# Revit family: Grohe_PlumbingFixtures_RapidoSmartBox_UniversalRoughInBox_35600000_Metric1
name_source: partatom
category: Plumbing Fixtures
revit_build: Autodesk Revit 2016 (Build: 20150714_1515(x64)
units: mm (PartAtom-declared; Revit-internal decimal feet)

## family parameters
Cut with Voids When Loaded = No
Host = Face
OmniClass Number = 23.45.55.17
OmniClass Title = Mixing Faucets
Part Type = Normal
Room Calculation Point = No
Round Connector Dimension = Use Diameter
Shared = Yes

## types (1)
- 35600000
    ADACompliant = No
    Assembly Code = D2010
    AssetType = Fixed
    BIMObjectName = Grohe_PlumbingFixtures_RapidoSmartBox_UniversalRoughInBox_35600000_Metric
    CW Connection = Yes
    CWFU = 4.5
    ClassificationName = Uniclass2015
    Color = Blue & Grey
    Cost = 0 $
    Default Elevation = 0 mm  [stored 0 ft]
    Description = 3 outlets 1/2"
2 inlets below, 1/2"
installation depth 75-105 mm
connection unit in DR brass
pre-mounted flushing plug
stable build-in box and protective cover
fixing options for solid walls and dry 
cladding
gasket
without set for final installation
    DurationUnit = Years
    Ecojoy = No
    ExpectedLife = 0
    Features = 3 outlets 1/2"
2 inlets below, 1/2"
installation depth 75-105 mm
connection unit in DR brass
pre-mounted flushing plug
stable build-in box and protective cover
fixing options for solid walls and dry 
cladding
gasket
without set for final installation
    Finish = Plastic & Brass
    HW Connection = Yes
    HWFU = 4.5
    IfcExportAs = IfcPipeFitting
    IfcExportType = IfcPipeFittingType
    Keynote = N13
    LowEmittingMaterial = No
    Manufacturer = Grohe
    ManufacturerName = Grohe
    MasterformatNumber = 01 52 19
    MasterformatTitle = Sanitary Facilities
    Model = GROHE Rapido SmartBox Universal rough-in box, 1/2"
    ModelNumber = 35600000
    ModelReference = GROHE Rapido SmartBox Universal rough-in box, 1/2"
    NominalDepth = 0 mm  [stored 0 ft]
    NominalHeight = 0 mm  [stored 0 ft]
    NominalLength = 0 mm  [stored 0 ft]
    ProductDocumentationLink = https://www.grohe.co.uk
    ProductPageURL = https://www.grohe.co.uk
    ProductionYear = 2017
    Type Comments = 35600000
    TypeName = GROHE Rapido SmartBox Universal rough-in box, 1/2"
    URL = www.grohe.com
    Vent Connection = No
    WFU = 0
    WarrantyDurationUnit = Years
    Waste Connection = No
    _BSBibleVersion = 15
    _BimSpecGuid = 0
    _CurrentRevision = 1
    _DistributedBy = www.bimstore.co.uk

note: [stored X ft] marks values corroborated as IEEE doubles in the binary element streams (Revit-internal decimal feet)

## geometry (parser evidence)
native form markers: Blend x2, Sweep x4
no freeform markers — native parametric forms only
